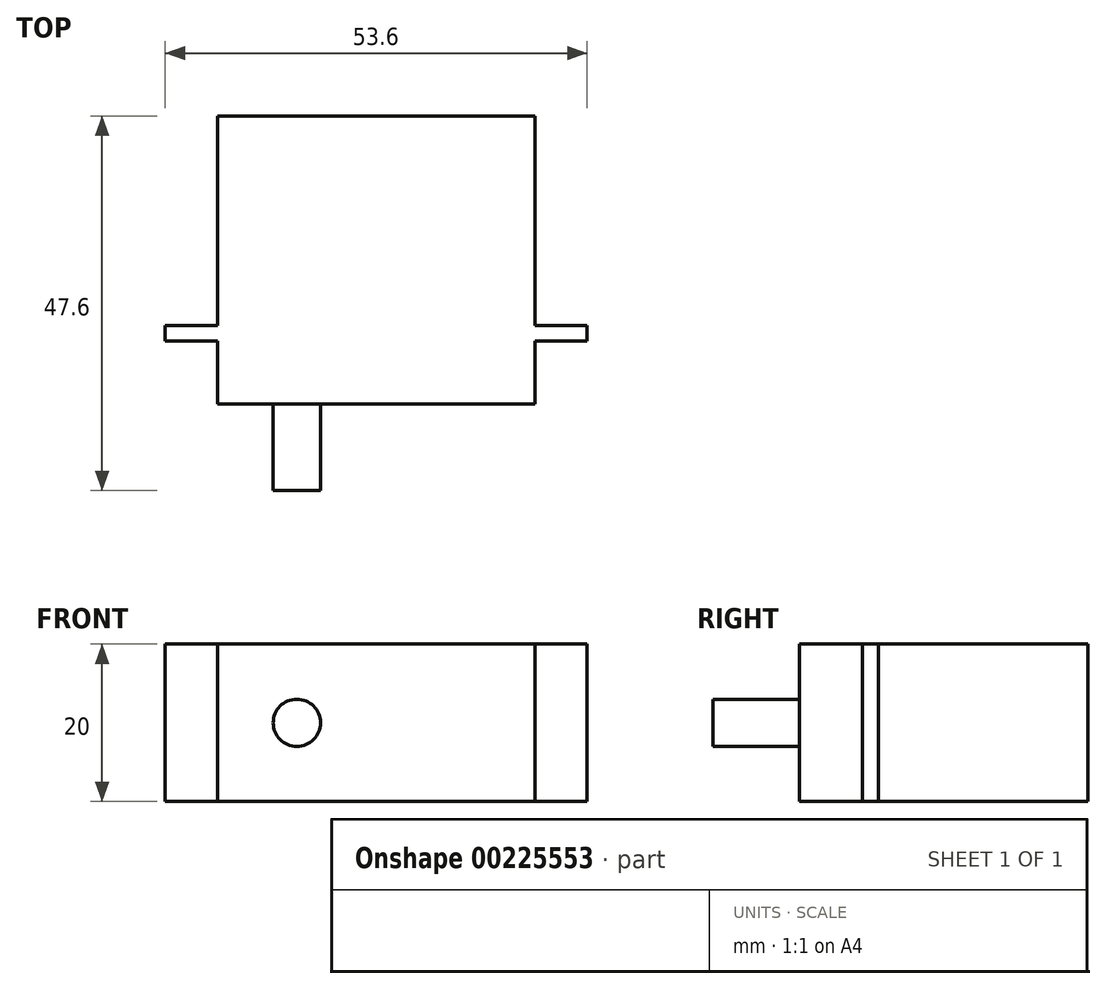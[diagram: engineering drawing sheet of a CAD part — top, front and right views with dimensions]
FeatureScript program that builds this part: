
annotation { "Feature Type Name" : "Feature", "Feature Type Description" : "" }
export const myFeature = defineFeature(function(context is Context, id is Id, definition is map)
    precondition{}
    {
        {
            var Q0;
            Q0=qCreatedBy(makeId("Front.planeOp"),FACE);
            var sketch = newSketch(context, id + "F0", { "sketchPlane" : qUnion([Q0])});
            skLineSegment(sketch, "E0.bottom", {"start": v(-20.15, 10) * mm, "end": v(20.15, 10) * mm});
            skLineSegment(sketch, "E0.top", {"start": v(-20.15, -10) * mm, "end": v(20.15, -10) * mm});
            skLineSegment(sketch, "E0.left", {"start": v(-20.15, 10) * mm, "end": v(-20.15, -10) * mm});
            skLineSegment(sketch, "E0.right", {"start": v(20.15, 10) * mm, "end": v(20.15, -10) * mm});
            skLineSegment(sketch, "E1", {"start": v(0, 10) * mm, "end": v(0, -10) * mm, "construction": true});
            skLineSegment(sketch, "E2", {"start": v(20.15, 0) * mm, "end": v(-20.15, 0) * mm, "construction": true});
            skPoint(sketch, "E3", {"position": v(0, 0) * mm});
            skSolve(sketch);
        }
        {
            var Q0;
            Q0=makeQuery(id+"F0.imprint","IMPRINT",FACE,{"disambiguationData":[TD([[makeQuery(id+"F0.imprint","IMPRINT",EDGE,{"derivedFrom":sQuery(id+"F0.wireOp",EDGE,"E0.bottom")}),-1.0]])]});
            extrude(context, id + "F1", {"entities" : qUnion([Q0]), "oppositeDirection" : true, "depth" : 36.6 * mm});
        }
        {
            var Q0;
            Q0=makeQuery(id+"F1.opExtrude","CAP_FACE",FACE,{"disambiguationData":[OSD([sQuery(id+"F0.wireOp",EDGE,"E0.bottom"),sQuery(id+"F0.wireOp",EDGE,"E0.top"),sQuery(id+"F0.wireOp",EDGE,"E0.left"),sQuery(id+"F0.wireOp",EDGE,"E0.right")])],"isStart":false});
            cPlane(context, id + "F2", {"entities" : qUnion([Q0]), "cplaneType" : CPlaneType.OFFSET, "offset" : 26.6 * mm, "oppositeDirection" : true, "width" : 150 * mm, "height" : 150 * mm});
        }
        {
            var Q0;
            Q0=qCreatedBy(id+"F2.planeOp",FACE);
            var sketch = newSketch(context, id + "F3", { "sketchPlane" : qUnion([Q0])});
            skLineSegment(sketch, "E4.0", {"start": v(20.15, 10) * mm, "end": v(20.15, -10) * mm});
            skLineSegment(sketch, "E5.0", {"start": v(-20.15, 10) * mm, "end": v(-20.15, -10) * mm});
            skLineSegment(sketch, "E6.0", {"start": v(0, 10) * mm, "end": v(0, -10) * mm});
            skLineSegment(sketch, "E7.bottom", {"start": v(20.15, 10) * mm, "end": v(-26.8, 10) * mm});
            skLineSegment(sketch, "E7.top", {"start": v(20.15, -10) * mm, "end": v(-26.8, -10) * mm});
            skLineSegment(sketch, "E7.right", {"start": v(-26.8, 10) * mm, "end": v(-26.8, -10) * mm});
            skLineSegment(sketch, "E8.MirrorCS", {"start": v(-20.15, 10) * mm, "end": v(26.8, 10) * mm});
            skLineSegment(sketch, "E9.MirrorCS", {"start": v(26.8, 10) * mm, "end": v(26.8, -10) * mm});
            skLineSegment(sketch, "E10.MirrorCS", {"start": v(-20.15, -10) * mm, "end": v(26.8, -10) * mm});
            skSolve(sketch);
        }
        {
            var Q0;
            Q0=makeQuery(id+"F3.imprint","IMPRINT",FACE,{"disambiguationData":[TD([[makeQuery(id+"F3.imprint","IMPRINT",EDGE,{"derivedFrom":sQuery(id+"F3.wireOp",EDGE,"E5.0")}),-1.0]])]});
            var Q1;
            {var subQ0=sQuery(id+"F3.wireOp",EDGE,"E4.0");Q1=makeQuery(id+"F3.imprint","IMPRINT",FACE,{"disambiguationData":[TD([[makeQuery(id+"F3.imprint","IMPRINT",EDGE,{"derivedFrom":subQ0}),1.0]])]});}
            extrude(context, id + "F4", {"entities" : qUnion([Q0, Q1]), "operationType" : NewBodyOperationType.ADD, "oppositeDirection" : true, "depth" : 2 * mm});
        }
        {
            var Q0;
            Q0=makeQuery(id+"F1.opExtrude","CAP_FACE",FACE,{"disambiguationData":[OSD([sQuery(id+"F0.wireOp",EDGE,"E0.bottom"),sQuery(id+"F0.wireOp",EDGE,"E0.top"),sQuery(id+"F0.wireOp",EDGE,"E0.left"),sQuery(id+"F0.wireOp",EDGE,"E0.right")])],"isStart":false});
            cPlane(context, id + "F5", {"entities" : qUnion([Q0]), "cplaneType" : CPlaneType.OFFSET, "offset" : 47.6 * mm, "oppositeDirection" : true, "width" : 150 * mm, "height" : 150 * mm});
        }
        {
            var Q0;
            Q0=qCreatedBy(id+"F5.planeOp",FACE);
            var sketch = newSketch(context, id + "F6", { "sketchPlane" : qUnion([Q0])});
            skPoint(sketch, "E11.0", {"position": v(20.15, 0) * mm});
            skPoint(sketch, "E12.0", {"position": v(0, 0) * mm});
            skLineSegment(sketch, "E13", {"start": v(20.15, 0) * mm, "end": v(0, 0) * mm, "construction": true});
            skPoint(sketch, "E14", {"position": v(10.07, 0) * mm});
            skCircle(sketch, "E15", {"center": v(10.07, 0) * mm, "radius": 3 * mm});
            skSolve(sketch);
        }
        {
            var Q0;
            Q0=makeQuery(id+"F6.imprint","IMPRINT",FACE,{"disambiguationData":[TD([[makeQuery(id+"F6.imprint","IMPRINT",EDGE,{"derivedFrom":sQuery(id+"F6.wireOp",EDGE,"E15")}),1.0]])]});
            extrude(context, id + "F7", {"entities" : qUnion([Q0]), "operationType" : NewBodyOperationType.ADD, "endBound" : BoundingType.UP_TO_NEXT, "depth" : 25 * mm});
        }
    });
